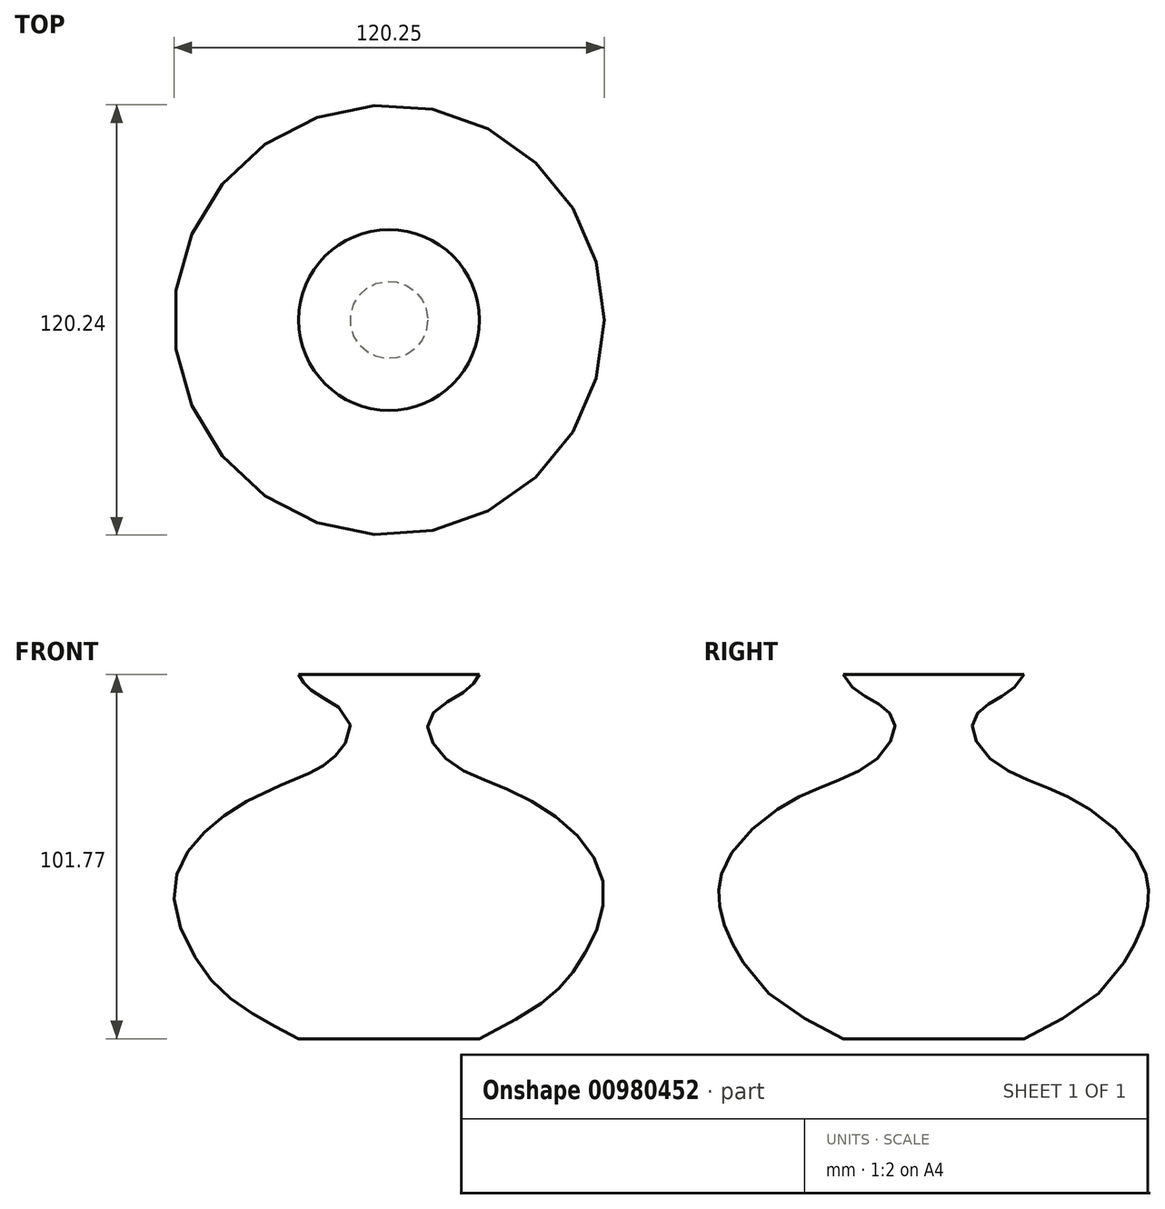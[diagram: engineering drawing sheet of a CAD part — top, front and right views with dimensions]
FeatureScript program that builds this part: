
annotation { "Feature Type Name" : "Feature", "Feature Type Description" : "" }
export const myFeature = defineFeature(function(context is Context, id is Id, definition is map)
    precondition{}
    {
        {
            var Q0;
            Q0=qCreatedBy(makeId("Front.planeOp"),FACE);
            var sketch = newSketch(context, id + "F0", { "sketchPlane" : qUnion([Q0])});
            skLineSegment(sketch, "E0", {"start": v(-31.43, 47.66) * mm, "end": v(-31.43, -54.1) * mm});
            skLineSegment(sketch, "E1", {"start": v(-31.43, -54.1) * mm, "end": v(-6.18, -54.1) * mm});
            skLineSegment(sketch, "E2", {"start": v(-31.43, 47.66) * mm, "end": v(-6.18, 47.66) * mm});
            skFitSpline(sketch, "E3", {"points": [v(-6.18, -54.1) * mm, v(21.1, -33.83) * mm, v(28.3, -9.68) * mm, v(7.1, 13) * mm, v(-15.02, 23.69) * mm, v(-20.19, 35.3) * mm, v(-10.05, 43.05) * mm, v(-6.18, 47.66) * mm], "startDerivative": vector(276.14, 138.07) * mm, "endDerivative": vector(33.35, 58.48) * mm});
            skSolve(sketch);
        }
        {
            var Q0;
            Q0=makeQuery(id+"F0.imprint","IMPRINT",FACE,{"disambiguationData":[TD([[makeQuery(id+"F0.imprint","IMPRINT",EDGE,{"derivedFrom":sQuery(id+"F0.wireOp",EDGE,"E0")}),1.0]])]});
            var Q1;
            Q1=sQuery(id+"F0.wireOp",EDGE,"E0");
            revolve(context, id + "F1", {"surfaceOperationType" : NewSurfaceOperationType.NEW, "entities" : qUnion([Q0]), "axis" : qUnion([Q1]), "revolveType" : RevolveType.FULL});
        }
    });
